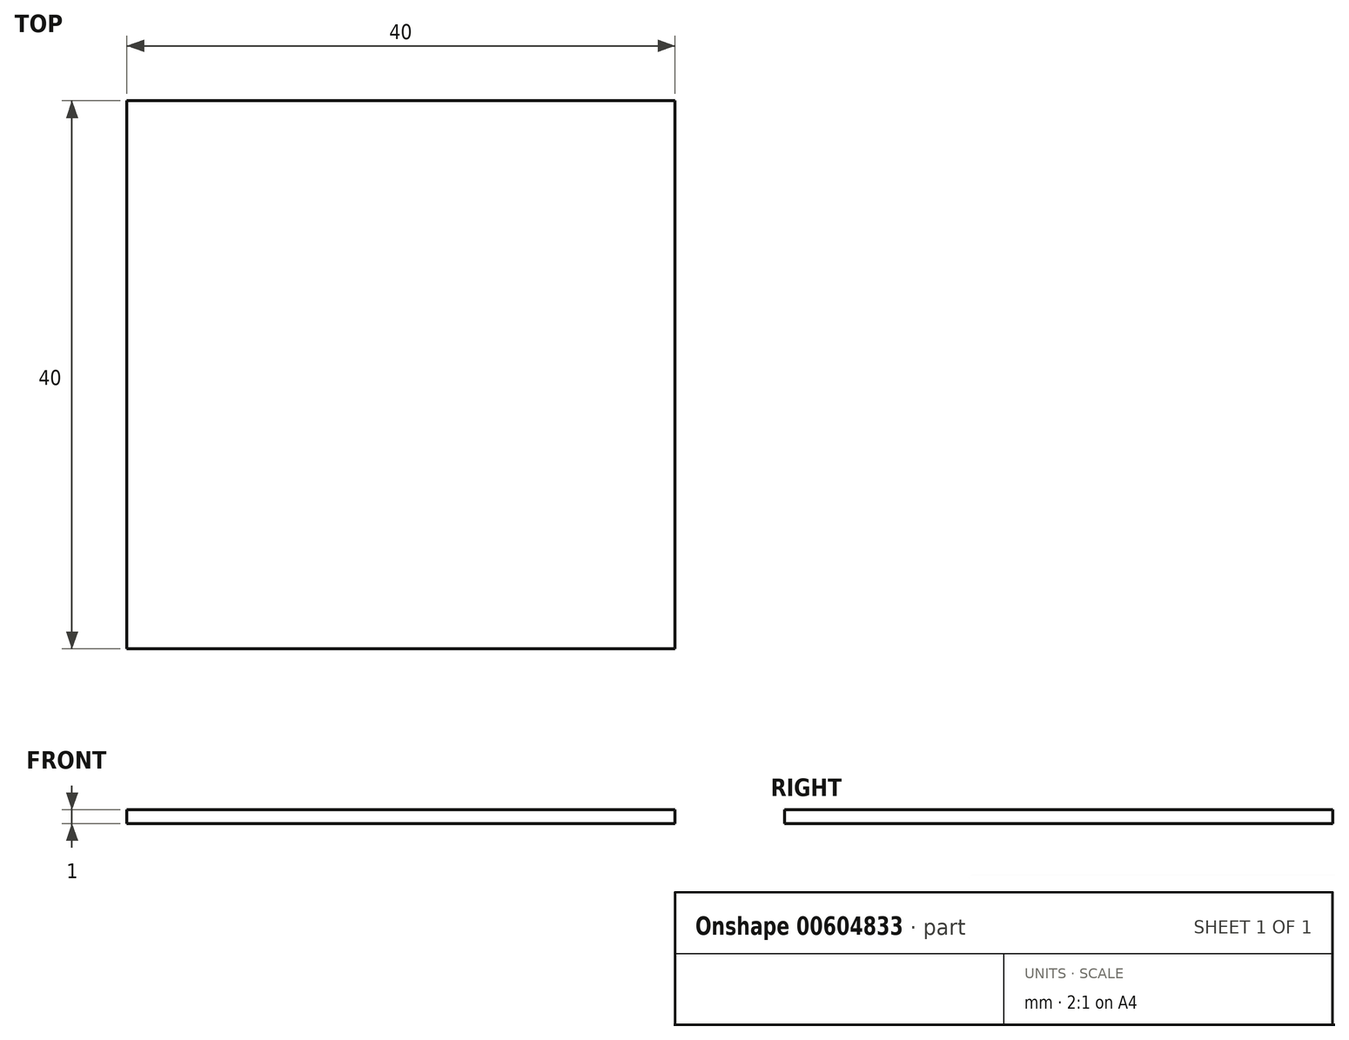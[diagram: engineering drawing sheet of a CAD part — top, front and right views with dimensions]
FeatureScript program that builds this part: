
annotation { "Feature Type Name" : "Feature", "Feature Type Description" : "" }
export const myFeature = defineFeature(function(context is Context, id is Id, definition is map)
    precondition{}
    {
        {
            var Q0;
            Q0=qCreatedBy(makeId("Top.planeOp"),FACE);
            var sketch = newSketch(context, id + "F0", { "sketchPlane" : qUnion([Q0])});
            skLineSegment(sketch, "E0.bottom", {"start": v(20, 20) * mm, "end": v(-20, 20) * mm});
            skLineSegment(sketch, "E0.top", {"start": v(20, -20) * mm, "end": v(-20, -20) * mm});
            skLineSegment(sketch, "E0.left", {"start": v(20, 20) * mm, "end": v(20, -20) * mm});
            skLineSegment(sketch, "E0.right", {"start": v(-20, 20) * mm, "end": v(-20, -20) * mm});
            skPoint(sketch, "E0.middle", {"position": v(0, 0) * mm});
            skSolve(sketch);
        }
        {
            var Q0;
            Q0=makeQuery(id+"F0.imprint","IMPRINT",FACE,{"disambiguationData":[TD([[makeQuery(id+"F0.imprint","IMPRINT",EDGE,{"derivedFrom":sQuery(id+"F0.wireOp",EDGE,"E0.bottom")}),1.0]])]});
            extrude(context, id + "F1", {"entities" : qUnion([Q0]), "depth" : 1 * mm, "offsetDistance" : 25.4 * mm});
        }
    });
